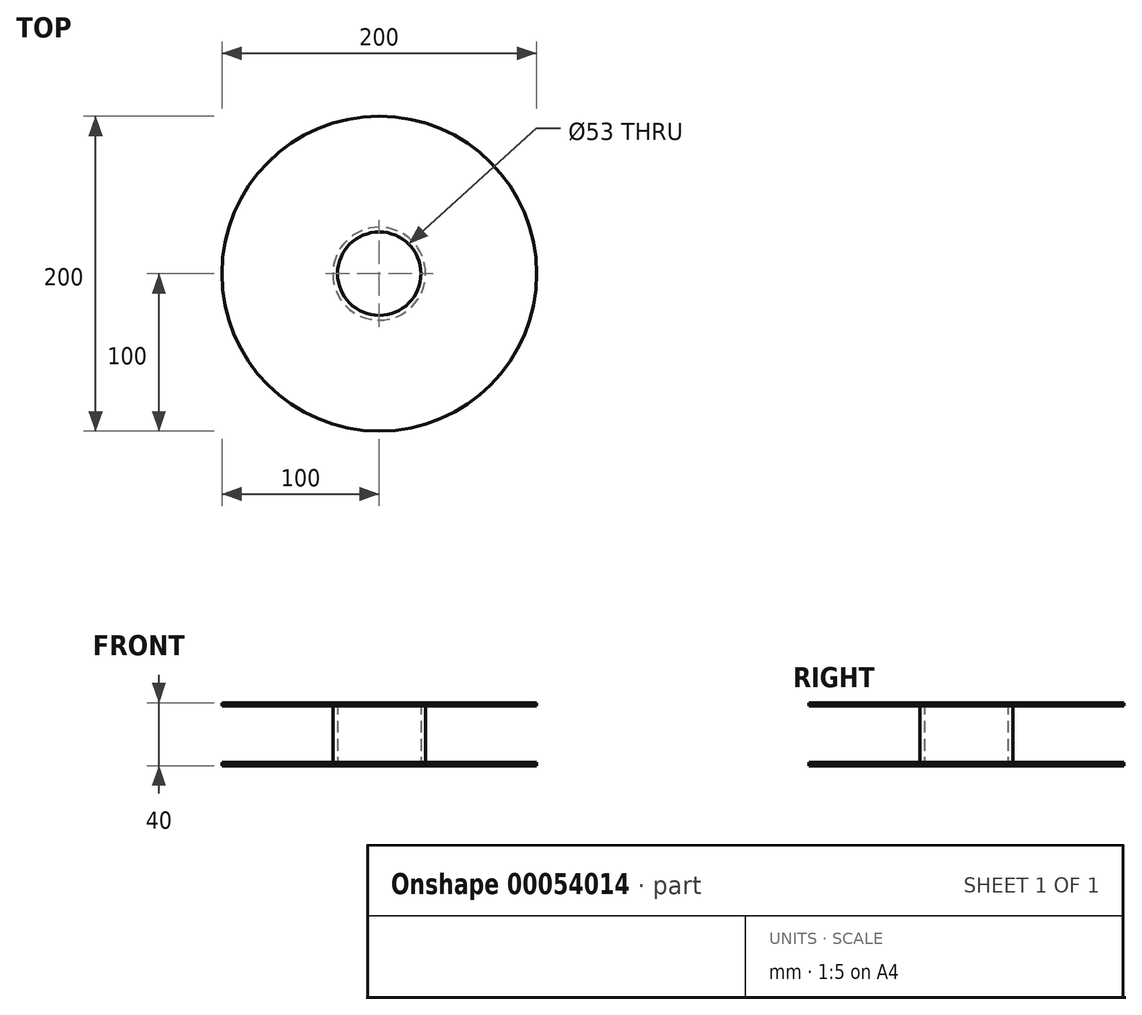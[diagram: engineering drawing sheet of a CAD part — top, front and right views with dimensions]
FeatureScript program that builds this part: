
annotation { "Feature Type Name" : "Feature", "Feature Type Description" : "" }
export const myFeature = defineFeature(function(context is Context, id is Id, definition is map)
    precondition{}
    {
        {
            var Q0;
            Q0=qCreatedBy(makeId("Front.planeOp"),FACE);
            var sketch = newSketch(context, id + "F0", { "sketchPlane" : qUnion([Q0])});
            skLineSegment(sketch, "E0", {"start": v(26.5, 40) * mm, "end": v(26.5, 0) * mm});
            skLineSegment(sketch, "E1", {"start": v(26.5, 0) * mm, "end": v(100, 0) * mm});
            skLineSegment(sketch, "E2", {"start": v(100, 0) * mm, "end": v(100, 2) * mm});
            skLineSegment(sketch, "E3", {"start": v(100, 2) * mm, "end": v(29.5, 2) * mm});
            skLineSegment(sketch, "E4", {"start": v(29.5, 2) * mm, "end": v(29.5, 38) * mm});
            skLineSegment(sketch, "E5", {"start": v(29.5, 38) * mm, "end": v(100, 38) * mm});
            skLineSegment(sketch, "E6", {"start": v(100, 38) * mm, "end": v(100, 40) * mm});
            skLineSegment(sketch, "E7", {"start": v(100, 40) * mm, "end": v(26.5, 40) * mm});
            skLineSegment(sketch, "E8", {"start": v(0, 0) * mm, "end": v(0, 23.08) * mm, "construction": true});
            skSolve(sketch);
        }
        {
            var Q0;
            Q0 = qSketchRegion(id + "F0", true);
            var Q1;
            Q1=sQuery(id+"F0.wireOp",EDGE,"E8");
            revolve(context, id + "F1", {"entities" : qUnion([Q0]), "axis" : qUnion([Q1]), "revolveType" : RevolveType.FULL});
        }
    });
